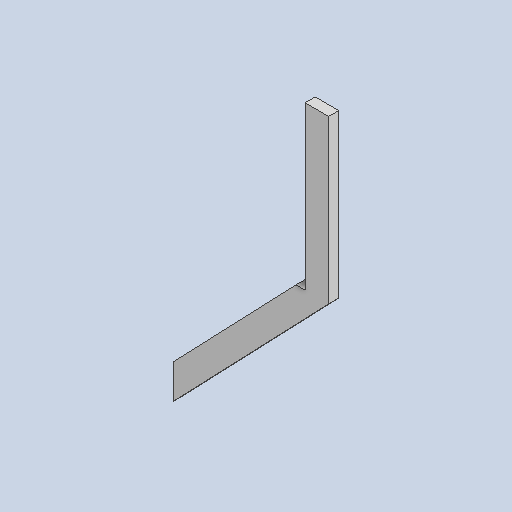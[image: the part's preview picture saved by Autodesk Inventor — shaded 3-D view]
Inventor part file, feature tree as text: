
AUTODESK INVENTOR PART (.ipt)
format: ipt  version: 2025 (Build 290162000, 162)  size: 140,288 bytes
history: native  units: in
note: dims shown in document units (in); Inventor stores cm internally (conversion verified against a paired STEP export)
features: other x5, reference x3, extrude x1, sketch x1
ambient origin geometry x8: Origin, YZ Plane, XZ Plane, XY Plane, X Axis, Y Axis, Z Axis, Center Point
bodies: Solid1 (feature_tree)
feature tree (10):
  extrude  "Extrusion1"  [1 undecoded]
  sketch  "Sketch1"  dims[d2=1.5in d3=0.0in]
  reference  "Reference1"
  reference  "Reference2"
  reference  "Reference3"
  other  "<userpath>\Documents\Tburn24\F_Legs2\F_Legs2.iam"
  other  "F_Legs2.iam"
  other  "8'x2x4:4"
  other  "4x2x4:6"
  other  "3'5x2x4:4"
note: 1 required parameter value undecoded (feature->parameter linkage not recoverable at this tier; creation-order binding heuristic only, values carry confidence <= 0.55)
